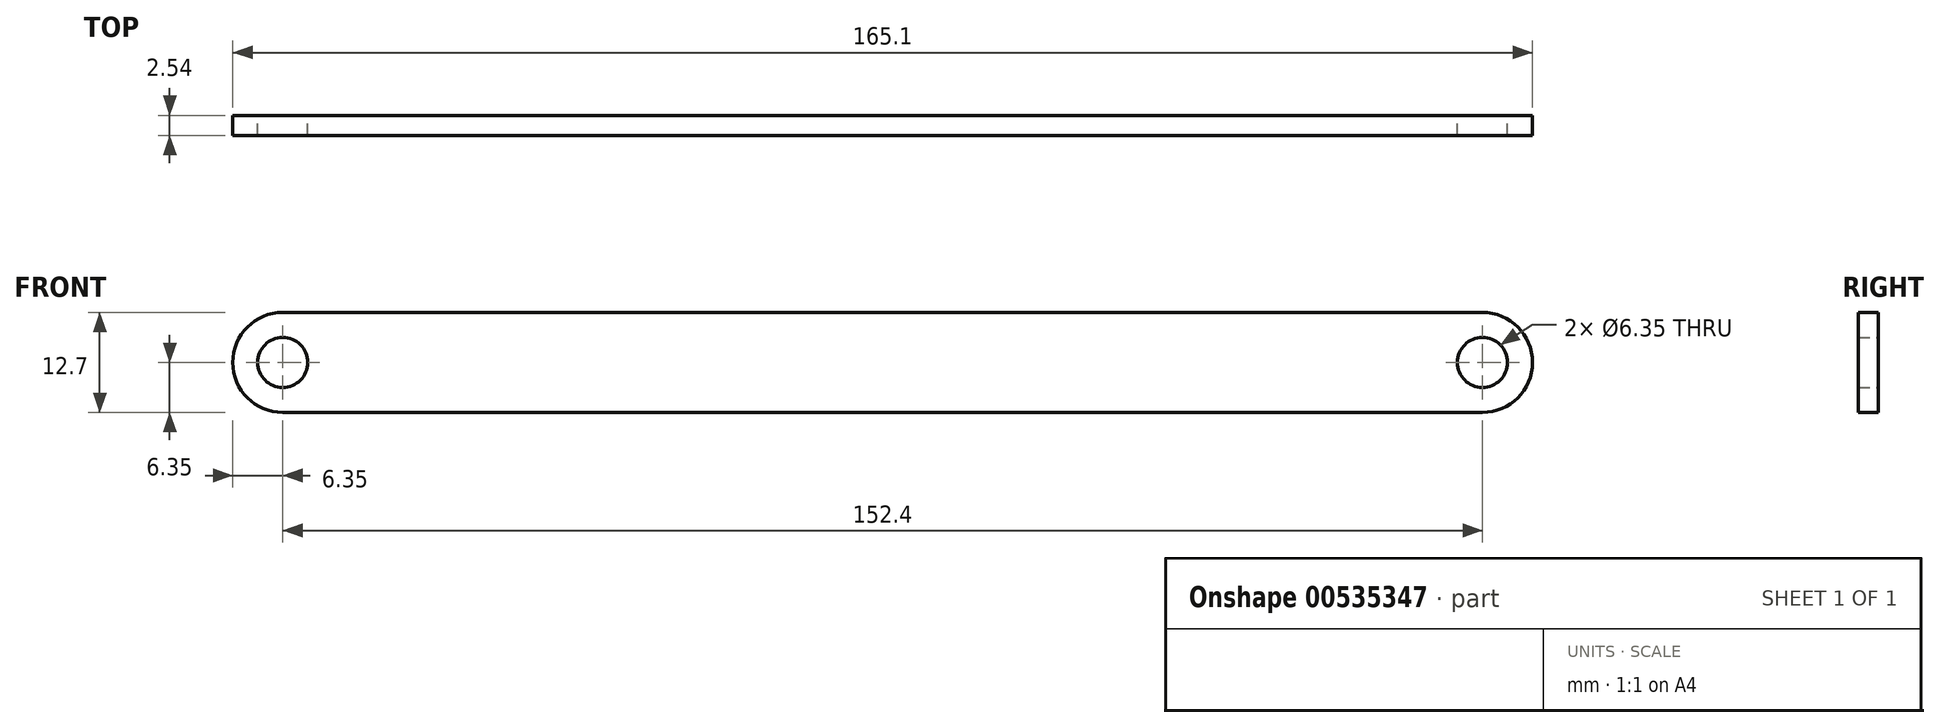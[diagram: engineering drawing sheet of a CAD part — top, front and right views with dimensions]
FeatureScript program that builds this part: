
annotation { "Feature Type Name" : "Feature", "Feature Type Description" : "" }
export const myFeature = defineFeature(function(context is Context, id is Id, definition is map)
    precondition{}
    {
        {
            var Q0;
            Q0=qCreatedBy(makeId("Front.planeOp"),FACE);
            var sketch = newSketch(context, id + "F0", { "sketchPlane" : qUnion([Q0])});
            skLineSegment(sketch, "E0", {"start": v(-152.4, 6.35) * mm, "end": v(0, 6.35) * mm});
            skArc(sketch, "E1", {"start": v(0, 6.35) * mm, "mid": v(6.35, 0) * mm, "end": v(0, -6.35) * mm});
            skArc(sketch, "E2", {"start": v(-152.4, 6.35) * mm, "mid": v(-158.75, 0) * mm, "end": v(-152.4, -6.35) * mm});
            skLineSegment(sketch, "E3", {"start": v(-152.4, -6.35) * mm, "end": v(0, -6.35) * mm});
            skCircle(sketch, "E4", {"center": v(-152.4, 0) * mm, "radius": 3.18 * mm});
            skCircle(sketch, "E5", {"center": v(0, 0) * mm, "radius": 3.18 * mm});
            skLineSegment(sketch, "E6", {"start": v(-152.4, 0) * mm, "end": v(0, 0) * mm, "construction": true});
            skLineSegment(sketch, "E7", {"start": v(-152.4, 0) * mm, "end": v(-105.3, -144.94) * mm, "construction": true});
            skLineSegment(sketch, "E8", {"start": v(-105.3, -144.94) * mm, "end": v(0, 0) * mm, "construction": true});
            skLineSegment(sketch, "E9", {"start": v(-7.46, -10.27) * mm, "end": v(37.17, -42.7) * mm, "construction": true});
            skLineSegment(sketch, "E10", {"start": v(37.17, -42.7) * mm, "end": v(-53.2, -167.1) * mm, "construction": true});
            skLineSegment(sketch, "E11", {"start": v(-53.2, -167.1) * mm, "end": v(-97.84, -134.67) * mm, "construction": true});
            skSolve(sketch);
        }
        {
            var Q0;
            Q0 = qSketchRegion(id + "F0", true);
            extrude(context, id + "F1", {"entities" : qUnion([Q0]), "depth" : 2.54 * mm, "offsetDistance" : 25.4 * mm});
        }
    });
